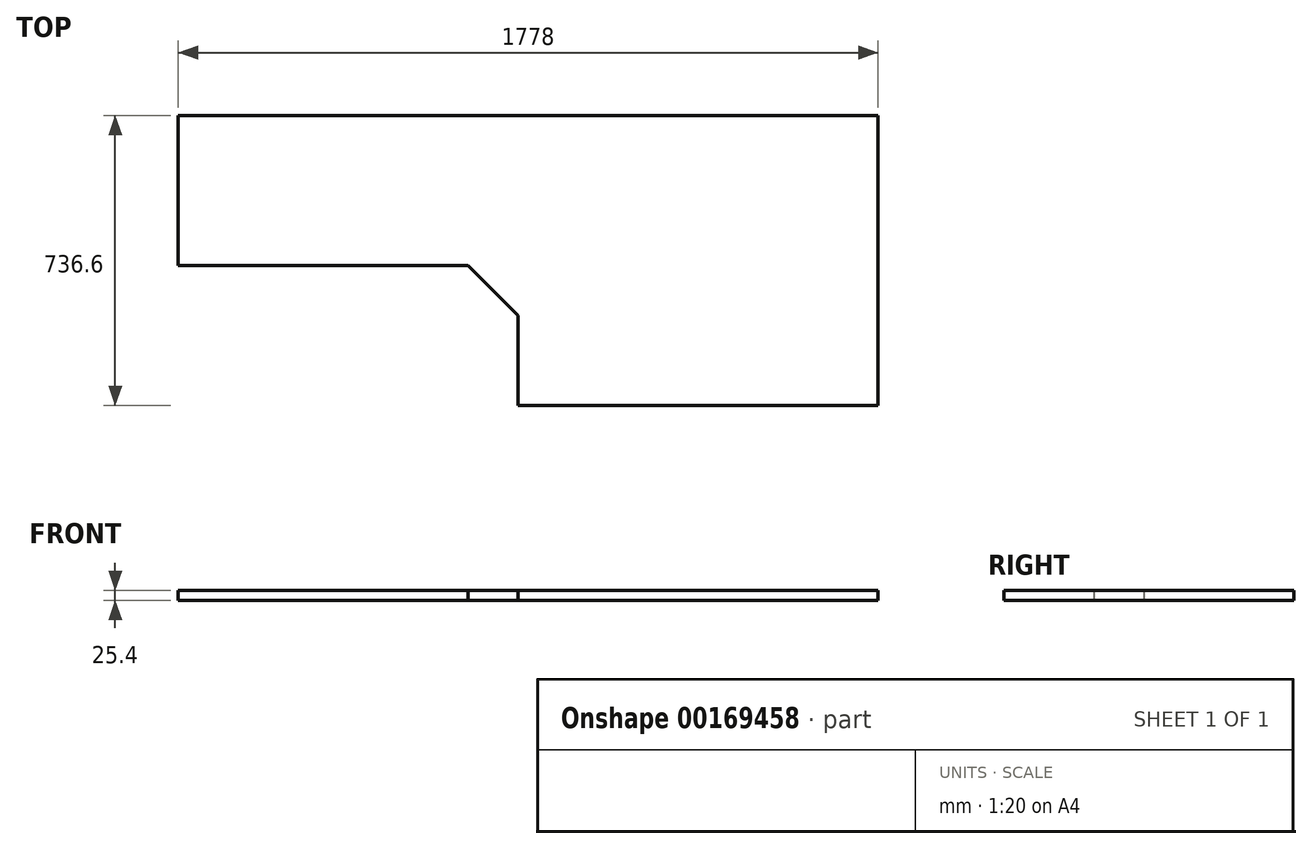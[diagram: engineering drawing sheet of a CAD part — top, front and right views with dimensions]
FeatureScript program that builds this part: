
annotation { "Feature Type Name" : "Feature", "Feature Type Description" : "" }
export const myFeature = defineFeature(function(context is Context, id is Id, definition is map)
    precondition{}
    {
        {
            var Q0;
            Q0=qCreatedBy(makeId("Top.planeOp"),FACE);
            var sketch = newSketch(context, id + "F0", { "sketchPlane" : qUnion([Q0])});
            skLineSegment(sketch, "E0.bottom", {"start": v(-1193.94, 295.36) * mm, "end": v(584.06, 295.36) * mm});
            skLineSegment(sketch, "E0.left", {"start": v(-1193.94, 295.36) * mm, "end": v(-1193.94, 291.06) * mm});
            skLineSegment(sketch, "E1.top", {"start": v(584.06, -441.24) * mm, "end": v(-330.34, -441.24) * mm});
            skLineSegment(sketch, "E1.left", {"start": v(584.06, 295.36) * mm, "end": v(584.06, -441.24) * mm});
            skLineSegment(sketch, "E2", {"start": v(-1193.94, 295.36) * mm, "end": v(-1193.94, -85.64) * mm});
            skLineSegment(sketch, "E3", {"start": v(-1193.94, -85.64) * mm, "end": v(-457.34, -85.64) * mm});
            skLineSegment(sketch, "E4", {"start": v(-330.34, -441.24) * mm, "end": v(-330.34, -212.64) * mm});
            skLineSegment(sketch, "E5", {"start": v(-330.34, -212.64) * mm, "end": v(-457.34, -85.64) * mm});
            skSolve(sketch);
        }
        {
            var Q0;
            Q0 = qSketchRegion(id + "F0", true);
            extrude(context, id + "F1", {"entities" : qUnion([Q0]), "depth" : 25.4 * mm});
        }
    });
